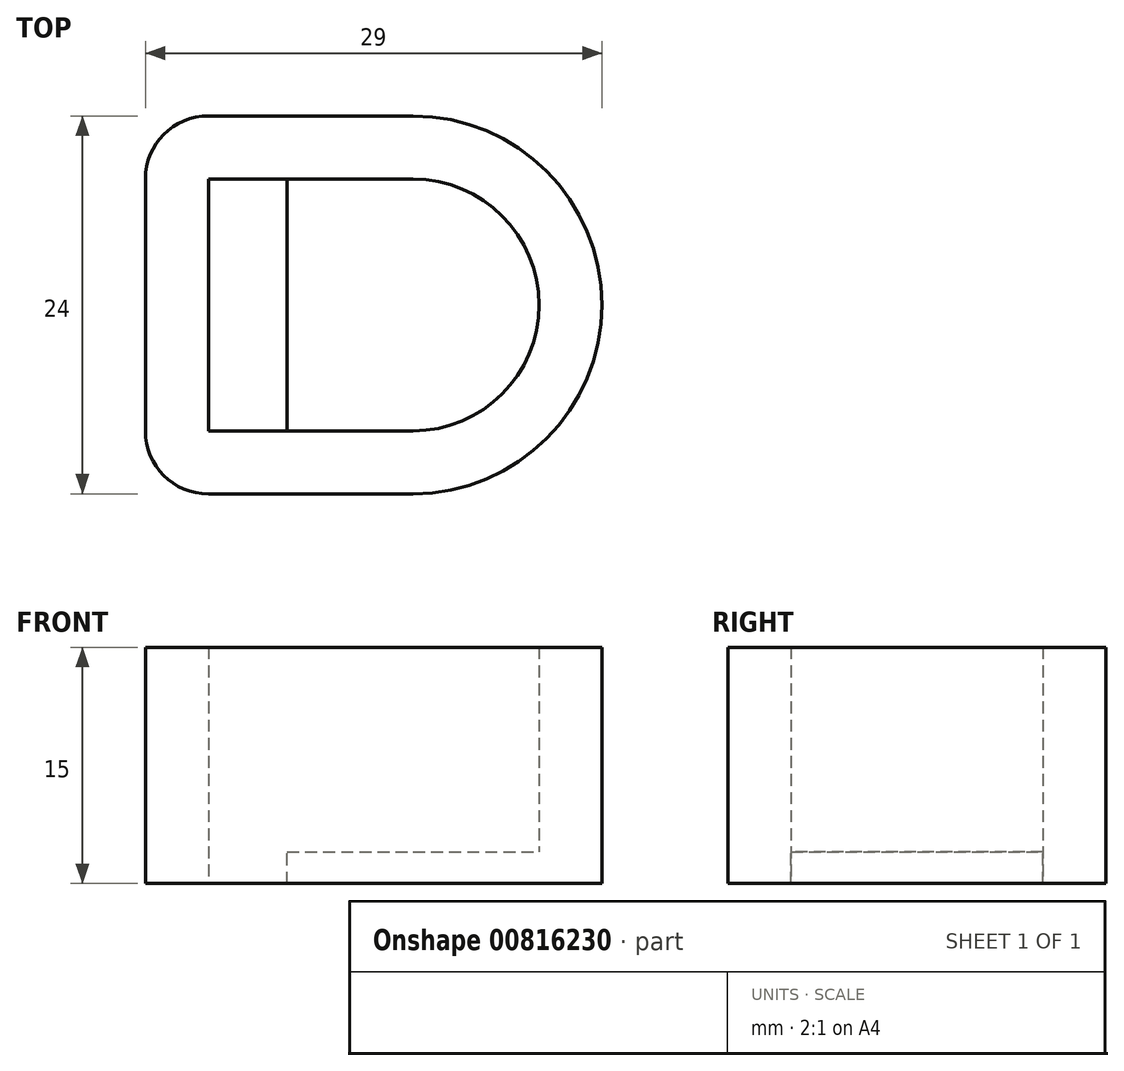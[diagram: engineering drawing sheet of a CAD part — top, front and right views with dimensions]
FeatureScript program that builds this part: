
annotation { "Feature Type Name" : "Feature", "Feature Type Description" : "" }
export const myFeature = defineFeature(function(context is Context, id is Id, definition is map)
    precondition{}
    {
        {
            var Q0;
            Q0=qCreatedBy(makeId("Top.planeOp"),FACE);
            var sketch = newSketch(context, id + "F0", { "sketchPlane" : qUnion([Q0])});
            skCircle(sketch, "E0", {"center": v(0, 0) * mm, "radius": 12 * mm});
            skLineSegment(sketch, "E1.bottom", {"start": v(-17, 12) * mm, "end": v(17, 12) * mm});
            skLineSegment(sketch, "E1.top", {"start": v(-17, -12) * mm, "end": v(17, -12) * mm});
            skLineSegment(sketch, "E1.left", {"start": v(-17, 12) * mm, "end": v(-17, -12) * mm});
            skLineSegment(sketch, "E1.right", {"start": v(17, 12) * mm, "end": v(17, -12) * mm});
            skSolve(sketch);
        }
        {
            var Q0;
            {var subQ5=sQuery(id+"F0.wireOp",EDGE,"E1.left");Q0=makeQuery(id+"F0.imprint","IMPRINT",FACE,{"disambiguationData":[TD([[makeQuery(id+"F0.imprint","IMPRINT",EDGE,{"derivedFrom":subQ5}),1.0]])]});}
            var Q1;
            {var subQ0=sQuery(id+"F0.wireOp",EDGE,"E0");var subQ1=makeQuery(id+"F0.imprint","INTERSECT",VERTEX,{"derivedFrom":[subQ0,sQuery(id+"F0.wireOp",EDGE,"E1.bottom")]});Q1=makeQuery(id+"F0.imprint","IMPRINT",FACE,{"disambiguationData":[TD([[makeQuery(id+"F0.imprint","IMPRINT",EDGE,{"disambiguationData":[TD([[subQ1,-1.0]])],"derivedFrom":subQ0}),1.0]])]});}
            extrude(context, id + "F1", {"entities" : qUnion([Q0, Q1]), "depth" : 2 * mm, "offsetDistance" : 25 * mm});
        }
        {
            var Q0;
            Q0=makeQuery(id+"F1.opExtrude","CAP_FACE",FACE,{"disambiguationData":[OSD([sQuery(id+"F0.wireOp",EDGE,"E0"),sQuery(id+"F0.wireOp",EDGE,"E1.bottom"),sQuery(id+"F0.wireOp",EDGE,"E1.top"),sQuery(id+"F0.wireOp",EDGE,"E1.left")])],"isStart":false});
            var sketch = newSketch(context, id + "F2", { "sketchPlane" : qUnion([Q0])});
            skCircle(sketch, "E2", {"center": v(0, 0) * mm, "radius": 8 * mm});
            skLineSegment(sketch, "E3.bottom", {"start": v(-13, 8) * mm, "end": v(13, 8) * mm});
            skLineSegment(sketch, "E3.top", {"start": v(-13, -8) * mm, "end": v(13, -8) * mm});
            skLineSegment(sketch, "E3.left", {"start": v(-13, 8) * mm, "end": v(-13, -8) * mm});
            skLineSegment(sketch, "E3.right", {"start": v(13, 8) * mm, "end": v(13, -8) * mm});
            skSolve(sketch);
        }
        {
            var Q0;
            {var subQ5=sQuery(id+"F2.wireOp",EDGE,"E3.left");Q0=makeQuery(id+"F2.imprint","IMPRINT",FACE,{"disambiguationData":[TD([[makeQuery(id+"F2.imprint","IMPRINT",EDGE,{"derivedFrom":subQ5}),-1.0]])]});}
            var Q1;
            {var subQ0=sQuery(id+"F2.wireOp",EDGE,"E3.bottom");var subQ1=sQuery(id+"F2.wireOp",EDGE,"E2");var subQ2=makeQuery(id+"F2.imprint","INTERSECT",VERTEX,{"derivedFrom":[subQ1,subQ0]});Q1=makeQuery(id+"F2.imprint","IMPRINT",FACE,{"disambiguationData":[TD([[makeQuery(id+"F2.imprint","IMPRINT",EDGE,{"disambiguationData":[TD([[subQ2,1.0]])],"derivedFrom":subQ1}),-1.0]])]});}
            extrude(context, id + "F3", {"entities" : qUnion([Q0, Q1]), "operationType" : NewBodyOperationType.ADD, "depth" : 13 * mm, "offsetDistance" : 25 * mm});
        }
        {
            var Q0;
            Q0=makeQuery(id+"F1.opExtrude","CAP_FACE",FACE,{"disambiguationData":[OSD([sQuery(id+"F0.wireOp",EDGE,"E0"),sQuery(id+"F0.wireOp",EDGE,"E1.bottom"),sQuery(id+"F0.wireOp",EDGE,"E1.top"),sQuery(id+"F0.wireOp",EDGE,"E1.left")])],"isStart":false});
            var sketch = newSketch(context, id + "F4", { "sketchPlane" : qUnion([Q0])});
            skLineSegment(sketch, "E4.bottom", {"start": v(-13, 8) * mm, "end": v(-8, 8) * mm});
            skLineSegment(sketch, "E4.top", {"start": v(-13, -8) * mm, "end": v(-8, -8) * mm});
            skLineSegment(sketch, "E4.left", {"start": v(-13, 8) * mm, "end": v(-13, -8) * mm});
            skLineSegment(sketch, "E4.right", {"start": v(-8, 8) * mm, "end": v(-8, -8) * mm});
            skSolve(sketch);
        }
        {
            var Q0;
            Q0=makeQuery(id+"F4.imprint","IMPRINT",FACE,{"disambiguationData":[TD([[makeQuery(id+"F4.imprint","IMPRINT",EDGE,{"derivedFrom":sQuery(id+"F4.wireOp",EDGE,"E4.bottom")}),-1.0]])]});
            extrude(context, id + "F5", {"entities" : qUnion([Q0]), "operationType" : NewBodyOperationType.REMOVE, "oppositeDirection" : true, "depth" : 25 * mm, "offsetDistance" : 25 * mm});
        }
        {
            var Q0;
            {var subQ0=sQuery(id+"F0.wireOp",EDGE,"E1.left");var subQ1=sQuery(id+"F0.wireOp",EDGE,"E1.bottom");Q0=makeQuery(id+"F3.boolean.opBoolean","MERGE",EDGE,{"derivedFrom":[makeQuery(id+"F1.opExtrude","SWEPT_EDGE",EDGE,{"disambiguationData":[OSD([subQ1,subQ0])]}),makeQuery(id+"F3.opExtrude","SWEPT_EDGE",EDGE,{"disambiguationData":[OSD([subQ1,subQ0])]})]});}
            var Q1;
            {var subQ0=sQuery(id+"F0.wireOp",EDGE,"E1.left");var subQ1=sQuery(id+"F0.wireOp",EDGE,"E1.top");Q1=makeQuery(id+"F3.boolean.opBoolean","MERGE",EDGE,{"derivedFrom":[makeQuery(id+"F1.opExtrude","SWEPT_EDGE",EDGE,{"disambiguationData":[OSD([subQ1,subQ0])]}),makeQuery(id+"F3.opExtrude","SWEPT_EDGE",EDGE,{"disambiguationData":[OSD([subQ1,subQ0])]})]});}
            fillet(context, id + "F6", {"entities" : qUnion([Q0, Q1]), "radius" : 4 * mm, "tangentPropagation" : true, "allowEdgeOverflow" : false});
        }
    });
